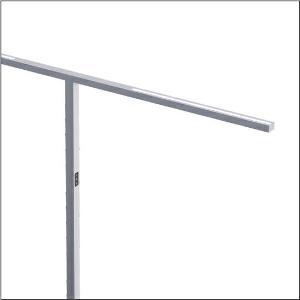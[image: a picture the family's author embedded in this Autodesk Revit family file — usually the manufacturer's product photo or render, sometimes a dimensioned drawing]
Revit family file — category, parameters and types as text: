
# Revit family: silica_31_floor_duo_51my52hmtcs
name_source: partatom
category: Lighting Fixtures
units: mm (PartAtom-declared; Revit-internal decimal feet)

## family parameters
Cut with Voids When Loaded = No
Host = Face
Light Source = No
Part Type = Normal
Room Calculation Point = No
Round Connector Dimension = Use Diameter
Shared = No

## types (1)
- --- (1 x LED, 17040 lm, 142 W, 4000K)
    Apparent Load = 142 VA
    CIE Flux Codes = 86 100 100 24 100
    Color Rendering = 80
    Color Temperature = 4000K
    Default Elevation = 1800 mm
    Description = Silica® 31 Floor duo, floorstanding luminaire, secondary optical cover: cover panel, of PMMA, light emission: direct/indirect distribution, primary light characteristic: symmetric, installation type: not mounted, LED, rated luminous flux: 17.040lm, luminous efficacy: 120lm/W, light colour: 8tw, colour temperature: 2700..6500K, control gear: Touchdim, daylight-dependent control, with cable with plug, mains connection: 230V, AC, 50Hz, connection cable included, cable length: 2,5m, rated input power: 142W, luminaire head, of aluminium, coated, metallic grey (RAL 9006), length: 2.372mm, width: 52mm, supporting column, angular, of aluminium, coated, silver, baseplate, of steel, coated, metallic grey (RAL 9006), local control - self-sufficient standalone sensors, direct and indirect component separately switchable, protection rating (complete): IP20, insulation class (complete): insulation class I (protective earthing), certification: CE, ENEC, permissible operating ambient temperature: -20..+40°C, standard: EN 50419, packaging unit: 1 piece
    Height = 36 mm
    Lamp = 1 x LED
    Lamp Light Flux = 17040 lm
    Lamp Power = 142 W
    Lamp count = 1
    Length = 2372 mm
    Luminous efficacy = 120 lm/W
    Manufacturer = Siteco
    ModVariant = No
    Model = 51MY52HMTCS
    Mounting Place = Floor
    Mounting Type = Freestanding
    Number of Poles = 1
    OnlyDefault = Yes
    Power Factor = 1
    Product Name = Silica 31 Floor duo
    Product group = floorstanding luminaire
    ProductGroupID = 1302
    Protection Class = Protection class I
    Protection Degree = IP 20
    RLX_Detail_Level = 1
    RLX_Emergency_Light_Flux = 0 lm
    RLX_Emergency_Type = 0
    RLX_Emergency_Type_DB = No
    RlxData = <blob elided: 17973 chars, md5=2839e5ae>
    Socket = socket
    Standby Power = 0 W
    System Light Flux = 17040 lm
    System Power = 142 W
    Type Comments = factory setting
    Type Image = l_1275342.jpg
    URL = http://relux.com
    VarID = @adj_088653
    Voltage = 0 V
    Weight = 0.00 kg
    Width = 52 mm  [stored 0.170604 ft]

note: [stored X ft] marks values corroborated as IEEE doubles in the binary element streams (Revit-internal decimal feet)

## geometry (parser evidence)
native form markers: Blend x4, Sweep x12
no freeform markers — native parametric forms only
